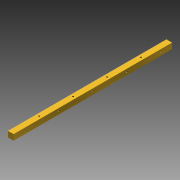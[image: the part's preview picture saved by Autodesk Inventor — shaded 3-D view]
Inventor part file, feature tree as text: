
AUTODESK INVENTOR PART (.ipt)
format: ipt  version: 2016 (Build 200138000, 138)  size: 98,816 bytes
history: native  units: in
note: dims shown in document units (in); Inventor stores cm internally (conversion verified against a paired STEP export)
features: sketch x3, hole x2, pattern_linear x2, extrude x1
ambient origin geometry x8: Origin, YZ Plane, XZ Plane, XY Plane, X Axis, Y Axis, Z Axis, Center Point
bodies: Solid1 (feature_tree)
feature tree (8):
  extrude  "Extrusion1"  Depth=0.25in
  hole  "Hole1"  [1 undecoded]
  pattern_linear  "Rectangular Pattern1"  Count1=5 Spacing1=1.5in
  pattern_linear  "Rectangular Pattern2"  Spacing1=0.75in  [1 undecoded]
  sketch  "Sketch1"  dims[d0=0.25in d2=0.25in]
  sketch  "Sketch2"  dims[d3=7.0in d4=0.0in d5=0.125in]
  sketch  "Sketch3"  dims[d6=0.5in d7=0.067in d8=0.75in d9=0.375in d10=0.25in d11=0.5635in d12=1.0in d13=0.8108in d21=1.9685in d23=1.5in d24=0.75in d27=0.8108in d28=0.5635in d29=0.25in d30=0.375in d31=1.0in d32=0.067in d33=1.25in d34=1.5748in d36=1.5in d37=0.125in]
  hole  "Hole2"  [1 undecoded]
note: 3 required parameter values undecoded (feature->parameter linkage not recoverable at this tier; creation-order binding heuristic only, values carry confidence <= 0.55)
